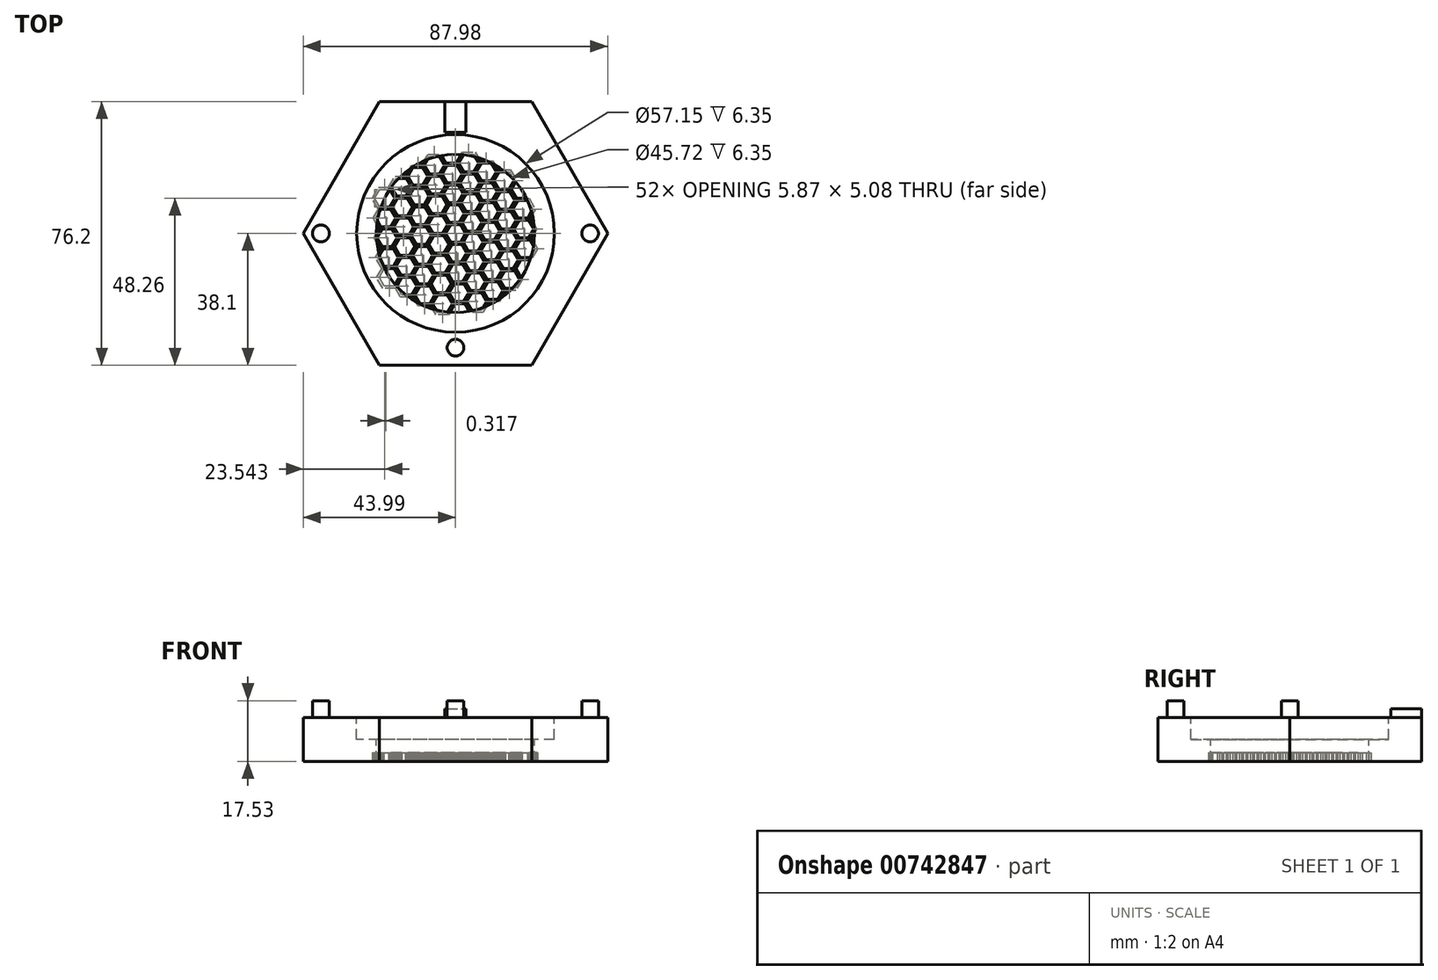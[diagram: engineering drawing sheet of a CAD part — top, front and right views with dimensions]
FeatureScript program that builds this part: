
annotation { "Feature Type Name" : "Feature", "Feature Type Description" : "" }
export const myFeature = defineFeature(function(context is Context, id is Id, definition is map)
    precondition{}
    {
        {
            var Q0;
            Q0=qCreatedBy(makeId("Top.planeOp"),FACE);
            var sketch = newSketch(context, id + "F0", { "sketchPlane" : qUnion([Q0])});
            skCircle(sketch, "E0.cCircle", {"center": v(0, 0) * mm, "radius": 38.1 * mm, "construction": true});
            skLineSegment(sketch, "E0.0", {"start": v(-22, 38.1) * mm, "end": v(22, 38.1) * mm});
            skLineSegment(sketch, "E0.1", {"start": v(22, 38.1) * mm, "end": v(44, 0) * mm});
            skLineSegment(sketch, "E0.2", {"start": v(44, 0) * mm, "end": v(22, -38.1) * mm});
            skLineSegment(sketch, "E0.3", {"start": v(22, -38.1) * mm, "end": v(-22, -38.1) * mm});
            skLineSegment(sketch, "E0.4", {"start": v(-22, -38.1) * mm, "end": v(-44, 0) * mm});
            skLineSegment(sketch, "E0.5", {"start": v(-44, 0) * mm, "end": v(-22, 38.1) * mm});
            skPoint(sketch, "E0.0.midPoint", {"position": v(0, 38.1) * mm});
            skSolve(sketch);
        }
        {
            var Q0;
            Q0 = qSketchRegion(id + "F0", true);
            extrude(context, id + "F1", {"entities" : qUnion([Q0]), "depth" : 12.7 * mm, "offsetDistance" : 25.4 * mm});
        }
        {
            var Q0;
            Q0=makeQuery(id+"F1.opExtrude","CAP_FACE",FACE,{"disambiguationData":[OSD([sQuery(id+"F0.wireOp",EDGE,"E0.0"),sQuery(id+"F0.wireOp",EDGE,"E0.1"),sQuery(id+"F0.wireOp",EDGE,"E0.2"),sQuery(id+"F0.wireOp",EDGE,"E0.3"),sQuery(id+"F0.wireOp",EDGE,"E0.4"),sQuery(id+"F0.wireOp",EDGE,"E0.5")])],"isStart":false});
            var sketch = newSketch(context, id + "F2", { "sketchPlane" : qUnion([Q0])});
            skCircle(sketch, "E1", {"center": v(0, 0) * mm, "radius": 28.58 * mm});
            skSolve(sketch);
        }
        {
            var Q0;
            Q0 = qSketchRegion(id + "F2", true);
            extrude(context, id + "F3", {"entities" : qUnion([Q0]), "operationType" : NewBodyOperationType.REMOVE, "oppositeDirection" : true, "depth" : 6.35 * mm, "offsetDistance" : 25.4 * mm});
        }
        {
            var Q0;
            Q0=makeQuery(id+"F3.boolean.opBoolean","COPY",FACE,{"derivedFrom":makeQuery(id+"F3.opExtrude","CAP_FACE",FACE,{"disambiguationData":[OSD([sQuery(id+"F2.wireOp",EDGE,"E1")])],"isStart":false})});
            var sketch = newSketch(context, id + "F4", { "sketchPlane" : qUnion([Q0])});
            skCircle(sketch, "E2", {"center": v(0, 0) * mm, "radius": 22.86 * mm});
            skSolve(sketch);
        }
        {
            var Q0;
            Q0 = qSketchRegion(id + "F4", true);
            extrude(context, id + "F5", {"entities" : qUnion([Q0]), "operationType" : NewBodyOperationType.REMOVE, "oppositeDirection" : true, "depth" : 25.4 * mm, "offsetDistance" : 25.4 * mm});
        }
        {
            var Q0;
            Q0=makeQuery(id+"F1.opExtrude","CAP_FACE",FACE,{"disambiguationData":[OSD([sQuery(id+"F0.wireOp",EDGE,"E0.0"),sQuery(id+"F0.wireOp",EDGE,"E0.1"),sQuery(id+"F0.wireOp",EDGE,"E0.2"),sQuery(id+"F0.wireOp",EDGE,"E0.3"),sQuery(id+"F0.wireOp",EDGE,"E0.4"),sQuery(id+"F0.wireOp",EDGE,"E0.5")])],"isStart":false});
            var sketch = newSketch(context, id + "F6", { "sketchPlane" : qUnion([Q0])});
            skCircle(sketch, "E3", {"center": v(0, -33.02) * mm, "radius": 2.41 * mm});
            skCircle(sketch, "E4", {"center": v(-38.91, 0) * mm, "radius": 2.41 * mm});
            skCircle(sketch, "E5", {"center": v(38.91, 0) * mm, "radius": 2.41 * mm});
            skSolve(sketch);
        }
        {
            var Q0;
            Q0 = qSketchRegion(id + "F6", true);
            extrude(context, id + "F7", {"entities" : qUnion([Q0]), "operationType" : NewBodyOperationType.ADD, "depth" : 4.83 * mm, "offsetDistance" : 25.4 * mm});
        }
        {
            var Q0;
            Q0=makeQuery(id+"F1.opExtrude","CAP_FACE",FACE,{"disambiguationData":[OSD([sQuery(id+"F0.wireOp",EDGE,"E0.0"),sQuery(id+"F0.wireOp",EDGE,"E0.1"),sQuery(id+"F0.wireOp",EDGE,"E0.2"),sQuery(id+"F0.wireOp",EDGE,"E0.3"),sQuery(id+"F0.wireOp",EDGE,"E0.4"),sQuery(id+"F0.wireOp",EDGE,"E0.5")])],"isStart":false});
            var sketch = newSketch(context, id + "F8", { "sketchPlane" : qUnion([Q0])});
            skLineSegment(sketch, "E6", {"start": v(0, 38.1) * mm, "end": v(-3.05, 38.1) * mm});
            skLineSegment(sketch, "E7", {"start": v(-3.05, 38.1) * mm, "end": v(-3.05, 29.21) * mm});
            skLineSegment(sketch, "E8", {"start": v(-3.05, 29.21) * mm, "end": v(3.05, 29.21) * mm});
            skLineSegment(sketch, "E9", {"start": v(3.05, 29.21) * mm, "end": v(3.05, 38.1) * mm});
            skLineSegment(sketch, "E10", {"start": v(3.05, 38.1) * mm, "end": v(0, 38.1) * mm});
            skSolve(sketch);
        }
        {
            var Q0;
            Q0 = qSketchRegion(id + "F8", true);
            extrude(context, id + "F9", {"entities" : qUnion([Q0]), "operationType" : NewBodyOperationType.ADD, "depth" : 2.54 * mm, "offsetDistance" : 25.4 * mm});
        }
        {
            var Q0;
            Q0=qCreatedBy(makeId("Top.planeOp"),FACE);
            var sketch = newSketch(context, id + "F10", { "sketchPlane" : qUnion([Q0])});
            skCircle(sketch, "E11.cCircle", {"center": v(0, 0) * mm, "radius": 3.18 * mm, "construction": true});
            skLineSegment(sketch, "E11.0", {"start": v(-1.83, 3.18) * mm, "end": v(1.83, 3.18) * mm});
            skLineSegment(sketch, "E11.1", {"start": v(1.83, 3.18) * mm, "end": v(3.67, 0) * mm});
            skLineSegment(sketch, "E11.2", {"start": v(3.67, 0) * mm, "end": v(1.83, -3.17) * mm});
            skLineSegment(sketch, "E11.3", {"start": v(1.83, -3.17) * mm, "end": v(-1.83, -3.18) * mm});
            skLineSegment(sketch, "E11.4", {"start": v(-1.83, -3.18) * mm, "end": v(-3.67, 0) * mm});
            skLineSegment(sketch, "E11.5", {"start": v(-3.67, 0) * mm, "end": v(-1.83, 3.18) * mm});
            skPoint(sketch, "E11.0.midPoint", {"position": v(0, 3.18) * mm});
            skSolve(sketch);
        }
        {
            var Q0;
            Q0 = qSketchRegion(id + "F10", true);
            extrude(context, id + "F11", {"entities" : qUnion([Q0]), "depth" : 2.54 * mm, "offsetDistance" : 25.4 * mm});
        }
        {
            var Q0;
            Q0=makeQuery(id+"F11.opExtrude","CAP_FACE",FACE,{"disambiguationData":[OSD([sQuery(id+"F10.wireOp",EDGE,"E11.0"),sQuery(id+"F10.wireOp",EDGE,"E11.1"),sQuery(id+"F10.wireOp",EDGE,"E11.2"),sQuery(id+"F10.wireOp",EDGE,"E11.3"),sQuery(id+"F10.wireOp",EDGE,"E11.4"),sQuery(id+"F10.wireOp",EDGE,"E11.5")])],"isStart":false});
            var sketch = newSketch(context, id + "F12", { "sketchPlane" : qUnion([Q0])});
            skCircle(sketch, "E12.cCircle", {"center": v(0, 0) * mm, "radius": 2.54 * mm, "construction": true});
            skLineSegment(sketch, "E12.0", {"start": v(-1.47, 2.54) * mm, "end": v(1.47, 2.54) * mm});
            skLineSegment(sketch, "E12.1", {"start": v(1.47, 2.54) * mm, "end": v(2.93, 0) * mm});
            skLineSegment(sketch, "E12.2", {"start": v(2.93, 0) * mm, "end": v(1.47, -2.54) * mm});
            skLineSegment(sketch, "E12.3", {"start": v(1.47, -2.54) * mm, "end": v(-1.47, -2.54) * mm});
            skLineSegment(sketch, "E12.4", {"start": v(-1.47, -2.54) * mm, "end": v(-2.93, 0) * mm});
            skLineSegment(sketch, "E12.5", {"start": v(-2.93, 0) * mm, "end": v(-1.47, 2.54) * mm});
            skPoint(sketch, "E12.0.midPoint", {"position": v(0, 2.54) * mm});
            skSolve(sketch);
        }
        {
            var Q0;
            Q0 = qSketchRegion(id + "F12", true);
            extrude(context, id + "F13", {"entities" : qUnion([Q0]), "operationType" : NewBodyOperationType.REMOVE, "oppositeDirection" : true, "depth" : 25.4 * mm, "offsetDistance" : 25.4 * mm});
        }
        {
            var Q0;
            Q0=makeQuery(id+"F11.opExtrude","SWEPT_BODY",BODY,{"disambiguationData":[OSD([sQuery(id+"F10.wireOp",EDGE,"E11.0"),sQuery(id+"F10.wireOp",EDGE,"E11.1"),sQuery(id+"F10.wireOp",EDGE,"E11.2"),sQuery(id+"F10.wireOp",EDGE,"E11.3"),sQuery(id+"F10.wireOp",EDGE,"E11.4"),sQuery(id+"F10.wireOp",EDGE,"E11.5")])]});
            transform(context, id + "F14", {"entities" : qUnion([Q0]), "transformType" : TransformType.TRANSLATION_3D, "dx" : 4.76 * mm, "dy" : 3.17 * mm, "dz" : 0 * mm, "makeCopy" : true});
        }
        {
            var Q0;
            Q0=makeQuery(id+"F11.opExtrude","SWEPT_BODY",BODY,{"disambiguationData":[OSD([sQuery(id+"F10.wireOp",EDGE,"E11.0"),sQuery(id+"F10.wireOp",EDGE,"E11.1"),sQuery(id+"F10.wireOp",EDGE,"E11.2"),sQuery(id+"F10.wireOp",EDGE,"E11.3"),sQuery(id+"F10.wireOp",EDGE,"E11.4"),sQuery(id+"F10.wireOp",EDGE,"E11.5")])]});
            var Q1;
            Q1=makeQuery(id+"F14.opPattern","COPY",BODY,{"derivedFrom":makeQuery(id+"F11.opExtrude","SWEPT_BODY",BODY,{"disambiguationData":[OSD([sQuery(id+"F10.wireOp",EDGE,"E11.0"),sQuery(id+"F10.wireOp",EDGE,"E11.1"),sQuery(id+"F10.wireOp",EDGE,"E11.2"),sQuery(id+"F10.wireOp",EDGE,"E11.3"),sQuery(id+"F10.wireOp",EDGE,"E11.4"),sQuery(id+"F10.wireOp",EDGE,"E11.5")])]}),"instanceName":"1"});
            transform(context, id + "F15", {"entities" : qUnion([Q0, Q1]), "transformType" : TransformType.TRANSLATION_3D, "dx" : -5.08 * mm, "dy" : 2.54 * mm, "dz" : 0 * mm, "makeCopy" : true});
        }
        {
            var Q0;
            Q0=makeQuery(id+"F15.opPattern","COPY",BODY,{"derivedFrom":makeQuery(id+"F14.opPattern","COPY",BODY,{"derivedFrom":makeQuery(id+"F11.opExtrude","SWEPT_BODY",BODY,{"disambiguationData":[OSD([sQuery(id+"F10.wireOp",EDGE,"E11.0"),sQuery(id+"F10.wireOp",EDGE,"E11.1"),sQuery(id+"F10.wireOp",EDGE,"E11.2"),sQuery(id+"F10.wireOp",EDGE,"E11.3"),sQuery(id+"F10.wireOp",EDGE,"E11.4"),sQuery(id+"F10.wireOp",EDGE,"E11.5")])]}),"instanceName":"1"}),"instanceName":"1"});
            var Q1;
            Q1=makeQuery(id+"F14.opPattern","COPY",BODY,{"derivedFrom":makeQuery(id+"F11.opExtrude","SWEPT_BODY",BODY,{"disambiguationData":[OSD([sQuery(id+"F10.wireOp",EDGE,"E11.0"),sQuery(id+"F10.wireOp",EDGE,"E11.1"),sQuery(id+"F10.wireOp",EDGE,"E11.2"),sQuery(id+"F10.wireOp",EDGE,"E11.3"),sQuery(id+"F10.wireOp",EDGE,"E11.4"),sQuery(id+"F10.wireOp",EDGE,"E11.5")])]}),"instanceName":"1"});
            var Q2;
            Q2=makeQuery(id+"F15.opPattern","COPY",BODY,{"derivedFrom":makeQuery(id+"F11.opExtrude","SWEPT_BODY",BODY,{"disambiguationData":[OSD([sQuery(id+"F10.wireOp",EDGE,"E11.0"),sQuery(id+"F10.wireOp",EDGE,"E11.1"),sQuery(id+"F10.wireOp",EDGE,"E11.2"),sQuery(id+"F10.wireOp",EDGE,"E11.3"),sQuery(id+"F10.wireOp",EDGE,"E11.4"),sQuery(id+"F10.wireOp",EDGE,"E11.5")])]}),"instanceName":"1"});
            var Q3;
            Q3=makeQuery(id+"F11.opExtrude","SWEPT_BODY",BODY,{"disambiguationData":[OSD([sQuery(id+"F10.wireOp",EDGE,"E11.0"),sQuery(id+"F10.wireOp",EDGE,"E11.1"),sQuery(id+"F10.wireOp",EDGE,"E11.2"),sQuery(id+"F10.wireOp",EDGE,"E11.3"),sQuery(id+"F10.wireOp",EDGE,"E11.4"),sQuery(id+"F10.wireOp",EDGE,"E11.5")])]});
            transform(context, id + "F16", {"entities" : qUnion([Q0, Q1, Q2, Q3]), "transformType" : TransformType.TRANSLATION_3D, "dx" : 9.52 * mm, "dy" : 6.35 * mm, "dz" : 0 * mm, "makeCopy" : true});
        }
        {
            var Q0;
            Q0=makeQuery(id+"F16.opPattern","COPY",BODY,{"derivedFrom":makeQuery(id+"F15.opPattern","COPY",BODY,{"derivedFrom":makeQuery(id+"F11.opExtrude","SWEPT_BODY",BODY,{"disambiguationData":[OSD([sQuery(id+"F10.wireOp",EDGE,"E11.0"),sQuery(id+"F10.wireOp",EDGE,"E11.1"),sQuery(id+"F10.wireOp",EDGE,"E11.2"),sQuery(id+"F10.wireOp",EDGE,"E11.3"),sQuery(id+"F10.wireOp",EDGE,"E11.4"),sQuery(id+"F10.wireOp",EDGE,"E11.5")])]}),"instanceName":"1"}),"instanceName":"1"});
            var Q1;
            Q1=makeQuery(id+"F11.opExtrude","SWEPT_BODY",BODY,{"disambiguationData":[OSD([sQuery(id+"F10.wireOp",EDGE,"E11.0"),sQuery(id+"F10.wireOp",EDGE,"E11.1"),sQuery(id+"F10.wireOp",EDGE,"E11.2"),sQuery(id+"F10.wireOp",EDGE,"E11.3"),sQuery(id+"F10.wireOp",EDGE,"E11.4"),sQuery(id+"F10.wireOp",EDGE,"E11.5")])]});
            var Q2;
            Q2=makeQuery(id+"F14.opPattern","COPY",BODY,{"derivedFrom":makeQuery(id+"F11.opExtrude","SWEPT_BODY",BODY,{"disambiguationData":[OSD([sQuery(id+"F10.wireOp",EDGE,"E11.0"),sQuery(id+"F10.wireOp",EDGE,"E11.1"),sQuery(id+"F10.wireOp",EDGE,"E11.2"),sQuery(id+"F10.wireOp",EDGE,"E11.3"),sQuery(id+"F10.wireOp",EDGE,"E11.4"),sQuery(id+"F10.wireOp",EDGE,"E11.5")])]}),"instanceName":"1"});
            var Q3;
            Q3=makeQuery(id+"F16.opPattern","COPY",BODY,{"derivedFrom":makeQuery(id+"F11.opExtrude","SWEPT_BODY",BODY,{"disambiguationData":[OSD([sQuery(id+"F10.wireOp",EDGE,"E11.0"),sQuery(id+"F10.wireOp",EDGE,"E11.1"),sQuery(id+"F10.wireOp",EDGE,"E11.2"),sQuery(id+"F10.wireOp",EDGE,"E11.3"),sQuery(id+"F10.wireOp",EDGE,"E11.4"),sQuery(id+"F10.wireOp",EDGE,"E11.5")])]}),"instanceName":"1"});
            var Q4;
            Q4=makeQuery(id+"F16.opPattern","COPY",BODY,{"derivedFrom":makeQuery(id+"F15.opPattern","COPY",BODY,{"derivedFrom":makeQuery(id+"F14.opPattern","COPY",BODY,{"derivedFrom":makeQuery(id+"F11.opExtrude","SWEPT_BODY",BODY,{"disambiguationData":[OSD([sQuery(id+"F10.wireOp",EDGE,"E11.0"),sQuery(id+"F10.wireOp",EDGE,"E11.1"),sQuery(id+"F10.wireOp",EDGE,"E11.2"),sQuery(id+"F10.wireOp",EDGE,"E11.3"),sQuery(id+"F10.wireOp",EDGE,"E11.4"),sQuery(id+"F10.wireOp",EDGE,"E11.5")])]}),"instanceName":"1"}),"instanceName":"1"}),"instanceName":"1"});
            var Q5;
            Q5=makeQuery(id+"F16.opPattern","COPY",BODY,{"derivedFrom":makeQuery(id+"F14.opPattern","COPY",BODY,{"derivedFrom":makeQuery(id+"F11.opExtrude","SWEPT_BODY",BODY,{"disambiguationData":[OSD([sQuery(id+"F10.wireOp",EDGE,"E11.0"),sQuery(id+"F10.wireOp",EDGE,"E11.1"),sQuery(id+"F10.wireOp",EDGE,"E11.2"),sQuery(id+"F10.wireOp",EDGE,"E11.3"),sQuery(id+"F10.wireOp",EDGE,"E11.4"),sQuery(id+"F10.wireOp",EDGE,"E11.5")])]}),"instanceName":"1"}),"instanceName":"1"});
            var Q6;
            Q6=makeQuery(id+"F15.opPattern","COPY",BODY,{"derivedFrom":makeQuery(id+"F14.opPattern","COPY",BODY,{"derivedFrom":makeQuery(id+"F11.opExtrude","SWEPT_BODY",BODY,{"disambiguationData":[OSD([sQuery(id+"F10.wireOp",EDGE,"E11.0"),sQuery(id+"F10.wireOp",EDGE,"E11.1"),sQuery(id+"F10.wireOp",EDGE,"E11.2"),sQuery(id+"F10.wireOp",EDGE,"E11.3"),sQuery(id+"F10.wireOp",EDGE,"E11.4"),sQuery(id+"F10.wireOp",EDGE,"E11.5")])]}),"instanceName":"1"}),"instanceName":"1"});
            var Q7;
            Q7=makeQuery(id+"F15.opPattern","COPY",BODY,{"derivedFrom":makeQuery(id+"F11.opExtrude","SWEPT_BODY",BODY,{"disambiguationData":[OSD([sQuery(id+"F10.wireOp",EDGE,"E11.0"),sQuery(id+"F10.wireOp",EDGE,"E11.1"),sQuery(id+"F10.wireOp",EDGE,"E11.2"),sQuery(id+"F10.wireOp",EDGE,"E11.3"),sQuery(id+"F10.wireOp",EDGE,"E11.4"),sQuery(id+"F10.wireOp",EDGE,"E11.5")])]}),"instanceName":"1"});
            transform(context, id + "F17", {"entities" : qUnion([Q0, Q1, Q2, Q3, Q4, Q5, Q6, Q7]), "transformType" : TransformType.TRANSLATION_3D, "dx" : 0.66 * mm, "dy" : -11.43 * mm, "dz" : 0 * mm, "makeCopy" : true});
        }
        {
            var Q0;
            Q0=makeQuery(id+"F17.opPattern","COPY",BODY,{"derivedFrom":makeQuery(id+"F15.opPattern","COPY",BODY,{"derivedFrom":makeQuery(id+"F14.opPattern","COPY",BODY,{"derivedFrom":makeQuery(id+"F11.opExtrude","SWEPT_BODY",BODY,{"disambiguationData":[OSD([sQuery(id+"F10.wireOp",EDGE,"E11.0"),sQuery(id+"F10.wireOp",EDGE,"E11.1"),sQuery(id+"F10.wireOp",EDGE,"E11.2"),sQuery(id+"F10.wireOp",EDGE,"E11.3"),sQuery(id+"F10.wireOp",EDGE,"E11.4"),sQuery(id+"F10.wireOp",EDGE,"E11.5")])]}),"instanceName":"1"}),"instanceName":"1"}),"instanceName":"1"});
            var Q1;
            Q1=makeQuery(id+"F17.opPattern","COPY",BODY,{"derivedFrom":makeQuery(id+"F14.opPattern","COPY",BODY,{"derivedFrom":makeQuery(id+"F11.opExtrude","SWEPT_BODY",BODY,{"disambiguationData":[OSD([sQuery(id+"F10.wireOp",EDGE,"E11.0"),sQuery(id+"F10.wireOp",EDGE,"E11.1"),sQuery(id+"F10.wireOp",EDGE,"E11.2"),sQuery(id+"F10.wireOp",EDGE,"E11.3"),sQuery(id+"F10.wireOp",EDGE,"E11.4"),sQuery(id+"F10.wireOp",EDGE,"E11.5")])]}),"instanceName":"1"}),"instanceName":"1"});
            var Q2;
            Q2=makeQuery(id+"F17.opPattern","COPY",BODY,{"derivedFrom":makeQuery(id+"F16.opPattern","COPY",BODY,{"derivedFrom":makeQuery(id+"F11.opExtrude","SWEPT_BODY",BODY,{"disambiguationData":[OSD([sQuery(id+"F10.wireOp",EDGE,"E11.0"),sQuery(id+"F10.wireOp",EDGE,"E11.1"),sQuery(id+"F10.wireOp",EDGE,"E11.2"),sQuery(id+"F10.wireOp",EDGE,"E11.3"),sQuery(id+"F10.wireOp",EDGE,"E11.4"),sQuery(id+"F10.wireOp",EDGE,"E11.5")])]}),"instanceName":"1"}),"instanceName":"1"});
            var Q3;
            Q3=makeQuery(id+"F17.opPattern","COPY",BODY,{"derivedFrom":makeQuery(id+"F16.opPattern","COPY",BODY,{"derivedFrom":makeQuery(id+"F15.opPattern","COPY",BODY,{"derivedFrom":makeQuery(id+"F11.opExtrude","SWEPT_BODY",BODY,{"disambiguationData":[OSD([sQuery(id+"F10.wireOp",EDGE,"E11.0"),sQuery(id+"F10.wireOp",EDGE,"E11.1"),sQuery(id+"F10.wireOp",EDGE,"E11.2"),sQuery(id+"F10.wireOp",EDGE,"E11.3"),sQuery(id+"F10.wireOp",EDGE,"E11.4"),sQuery(id+"F10.wireOp",EDGE,"E11.5")])]}),"instanceName":"1"}),"instanceName":"1"}),"instanceName":"1"});
            var Q4;
            Q4=makeQuery(id+"F17.opPattern","COPY",BODY,{"derivedFrom":makeQuery(id+"F16.opPattern","COPY",BODY,{"derivedFrom":makeQuery(id+"F15.opPattern","COPY",BODY,{"derivedFrom":makeQuery(id+"F14.opPattern","COPY",BODY,{"derivedFrom":makeQuery(id+"F11.opExtrude","SWEPT_BODY",BODY,{"disambiguationData":[OSD([sQuery(id+"F10.wireOp",EDGE,"E11.0"),sQuery(id+"F10.wireOp",EDGE,"E11.1"),sQuery(id+"F10.wireOp",EDGE,"E11.2"),sQuery(id+"F10.wireOp",EDGE,"E11.3"),sQuery(id+"F10.wireOp",EDGE,"E11.4"),sQuery(id+"F10.wireOp",EDGE,"E11.5")])]}),"instanceName":"1"}),"instanceName":"1"}),"instanceName":"1"}),"instanceName":"1"});
            var Q5;
            Q5=makeQuery(id+"F17.opPattern","COPY",BODY,{"derivedFrom":makeQuery(id+"F15.opPattern","COPY",BODY,{"derivedFrom":makeQuery(id+"F11.opExtrude","SWEPT_BODY",BODY,{"disambiguationData":[OSD([sQuery(id+"F10.wireOp",EDGE,"E11.0"),sQuery(id+"F10.wireOp",EDGE,"E11.1"),sQuery(id+"F10.wireOp",EDGE,"E11.2"),sQuery(id+"F10.wireOp",EDGE,"E11.3"),sQuery(id+"F10.wireOp",EDGE,"E11.4"),sQuery(id+"F10.wireOp",EDGE,"E11.5")])]}),"instanceName":"1"}),"instanceName":"1"});
            var Q6;
            Q6=makeQuery(id+"F17.opPattern","COPY",BODY,{"derivedFrom":makeQuery(id+"F16.opPattern","COPY",BODY,{"derivedFrom":makeQuery(id+"F14.opPattern","COPY",BODY,{"derivedFrom":makeQuery(id+"F11.opExtrude","SWEPT_BODY",BODY,{"disambiguationData":[OSD([sQuery(id+"F10.wireOp",EDGE,"E11.0"),sQuery(id+"F10.wireOp",EDGE,"E11.1"),sQuery(id+"F10.wireOp",EDGE,"E11.2"),sQuery(id+"F10.wireOp",EDGE,"E11.3"),sQuery(id+"F10.wireOp",EDGE,"E11.4"),sQuery(id+"F10.wireOp",EDGE,"E11.5")])]}),"instanceName":"1"}),"instanceName":"1"}),"instanceName":"1"});
            transform(context, id + "F18", {"entities" : qUnion([Q0, Q1, Q2, Q3, Q4, Q5, Q6]), "transformType" : TransformType.TRANSLATION_3D, "dx" : 0.64 * mm, "dy" : -11.43 * mm, "dz" : 0 * mm, "makeCopy" : true});
        }
        {
            var Q0;
            Q0=makeQuery(id+"F17.opPattern","COPY",BODY,{"derivedFrom":makeQuery(id+"F16.opPattern","COPY",BODY,{"derivedFrom":makeQuery(id+"F11.opExtrude","SWEPT_BODY",BODY,{"disambiguationData":[OSD([sQuery(id+"F10.wireOp",EDGE,"E11.0"),sQuery(id+"F10.wireOp",EDGE,"E11.1"),sQuery(id+"F10.wireOp",EDGE,"E11.2"),sQuery(id+"F10.wireOp",EDGE,"E11.3"),sQuery(id+"F10.wireOp",EDGE,"E11.4"),sQuery(id+"F10.wireOp",EDGE,"E11.5")])]}),"instanceName":"1"}),"instanceName":"1"});
            var Q1;
            Q1=makeQuery(id+"F17.opPattern","COPY",BODY,{"derivedFrom":makeQuery(id+"F16.opPattern","COPY",BODY,{"derivedFrom":makeQuery(id+"F14.opPattern","COPY",BODY,{"derivedFrom":makeQuery(id+"F11.opExtrude","SWEPT_BODY",BODY,{"disambiguationData":[OSD([sQuery(id+"F10.wireOp",EDGE,"E11.0"),sQuery(id+"F10.wireOp",EDGE,"E11.1"),sQuery(id+"F10.wireOp",EDGE,"E11.2"),sQuery(id+"F10.wireOp",EDGE,"E11.3"),sQuery(id+"F10.wireOp",EDGE,"E11.4"),sQuery(id+"F10.wireOp",EDGE,"E11.5")])]}),"instanceName":"1"}),"instanceName":"1"}),"instanceName":"1"});
            transform(context, id + "F19", {"entities" : qUnion([Q0, Q1]), "transformType" : TransformType.TRANSLATION_3D, "dx" : 5.08 * mm, "dy" : -2.54 * mm, "dz" : 0 * mm, "makeCopy" : true});
        }
        {
            var Q0;
            Q0=makeQuery(id+"F17.opPattern","COPY",BODY,{"derivedFrom":makeQuery(id+"F16.opPattern","COPY",BODY,{"derivedFrom":makeQuery(id+"F14.opPattern","COPY",BODY,{"derivedFrom":makeQuery(id+"F11.opExtrude","SWEPT_BODY",BODY,{"disambiguationData":[OSD([sQuery(id+"F10.wireOp",EDGE,"E11.0"),sQuery(id+"F10.wireOp",EDGE,"E11.1"),sQuery(id+"F10.wireOp",EDGE,"E11.2"),sQuery(id+"F10.wireOp",EDGE,"E11.3"),sQuery(id+"F10.wireOp",EDGE,"E11.4"),sQuery(id+"F10.wireOp",EDGE,"E11.5")])]}),"instanceName":"1"}),"instanceName":"1"}),"instanceName":"1"});
            var Q1;
            Q1=makeQuery(id+"F17.opPattern","COPY",BODY,{"derivedFrom":makeQuery(id+"F16.opPattern","COPY",BODY,{"derivedFrom":makeQuery(id+"F15.opPattern","COPY",BODY,{"derivedFrom":makeQuery(id+"F14.opPattern","COPY",BODY,{"derivedFrom":makeQuery(id+"F11.opExtrude","SWEPT_BODY",BODY,{"disambiguationData":[OSD([sQuery(id+"F10.wireOp",EDGE,"E11.0"),sQuery(id+"F10.wireOp",EDGE,"E11.1"),sQuery(id+"F10.wireOp",EDGE,"E11.2"),sQuery(id+"F10.wireOp",EDGE,"E11.3"),sQuery(id+"F10.wireOp",EDGE,"E11.4"),sQuery(id+"F10.wireOp",EDGE,"E11.5")])]}),"instanceName":"1"}),"instanceName":"1"}),"instanceName":"1"}),"instanceName":"1"});
            var Q2;
            Q2=makeQuery(id+"F16.opPattern","COPY",BODY,{"derivedFrom":makeQuery(id+"F15.opPattern","COPY",BODY,{"derivedFrom":makeQuery(id+"F14.opPattern","COPY",BODY,{"derivedFrom":makeQuery(id+"F11.opExtrude","SWEPT_BODY",BODY,{"disambiguationData":[OSD([sQuery(id+"F10.wireOp",EDGE,"E11.0"),sQuery(id+"F10.wireOp",EDGE,"E11.1"),sQuery(id+"F10.wireOp",EDGE,"E11.2"),sQuery(id+"F10.wireOp",EDGE,"E11.3"),sQuery(id+"F10.wireOp",EDGE,"E11.4"),sQuery(id+"F10.wireOp",EDGE,"E11.5")])]}),"instanceName":"1"}),"instanceName":"1"}),"instanceName":"1"});
            transform(context, id + "F20", {"entities" : qUnion([Q0, Q1, Q2]), "transformType" : TransformType.TRANSLATION_3D, "dx" : 4.78 * mm, "dy" : 3.17 * mm, "dz" : 0 * mm, "makeCopy" : true});
        }
        {
            var Q0;
            Q0=makeQuery(id+"F16.opPattern","COPY",BODY,{"derivedFrom":makeQuery(id+"F15.opPattern","COPY",BODY,{"derivedFrom":makeQuery(id+"F11.opExtrude","SWEPT_BODY",BODY,{"disambiguationData":[OSD([sQuery(id+"F10.wireOp",EDGE,"E11.0"),sQuery(id+"F10.wireOp",EDGE,"E11.1"),sQuery(id+"F10.wireOp",EDGE,"E11.2"),sQuery(id+"F10.wireOp",EDGE,"E11.3"),sQuery(id+"F10.wireOp",EDGE,"E11.4"),sQuery(id+"F10.wireOp",EDGE,"E11.5")])]}),"instanceName":"1"}),"instanceName":"1"});
            var Q1;
            Q1=makeQuery(id+"F14.opPattern","COPY",BODY,{"derivedFrom":makeQuery(id+"F11.opExtrude","SWEPT_BODY",BODY,{"disambiguationData":[OSD([sQuery(id+"F10.wireOp",EDGE,"E11.0"),sQuery(id+"F10.wireOp",EDGE,"E11.1"),sQuery(id+"F10.wireOp",EDGE,"E11.2"),sQuery(id+"F10.wireOp",EDGE,"E11.3"),sQuery(id+"F10.wireOp",EDGE,"E11.4"),sQuery(id+"F10.wireOp",EDGE,"E11.5")])]}),"instanceName":"1"});
            var Q2;
            Q2=makeQuery(id+"F16.opPattern","COPY",BODY,{"derivedFrom":makeQuery(id+"F11.opExtrude","SWEPT_BODY",BODY,{"disambiguationData":[OSD([sQuery(id+"F10.wireOp",EDGE,"E11.0"),sQuery(id+"F10.wireOp",EDGE,"E11.1"),sQuery(id+"F10.wireOp",EDGE,"E11.2"),sQuery(id+"F10.wireOp",EDGE,"E11.3"),sQuery(id+"F10.wireOp",EDGE,"E11.4"),sQuery(id+"F10.wireOp",EDGE,"E11.5")])]}),"instanceName":"1"});
            var Q3;
            Q3=makeQuery(id+"F19.opPattern","COPY",BODY,{"derivedFrom":makeQuery(id+"F17.opPattern","COPY",BODY,{"derivedFrom":makeQuery(id+"F16.opPattern","COPY",BODY,{"derivedFrom":makeQuery(id+"F14.opPattern","COPY",BODY,{"derivedFrom":makeQuery(id+"F11.opExtrude","SWEPT_BODY",BODY,{"disambiguationData":[OSD([sQuery(id+"F10.wireOp",EDGE,"E11.0"),sQuery(id+"F10.wireOp",EDGE,"E11.1"),sQuery(id+"F10.wireOp",EDGE,"E11.2"),sQuery(id+"F10.wireOp",EDGE,"E11.3"),sQuery(id+"F10.wireOp",EDGE,"E11.4"),sQuery(id+"F10.wireOp",EDGE,"E11.5")])]}),"instanceName":"1"}),"instanceName":"1"}),"instanceName":"1"}),"instanceName":"1"});
            var Q4;
            Q4=makeQuery(id+"F15.opPattern","COPY",BODY,{"derivedFrom":makeQuery(id+"F14.opPattern","COPY",BODY,{"derivedFrom":makeQuery(id+"F11.opExtrude","SWEPT_BODY",BODY,{"disambiguationData":[OSD([sQuery(id+"F10.wireOp",EDGE,"E11.0"),sQuery(id+"F10.wireOp",EDGE,"E11.1"),sQuery(id+"F10.wireOp",EDGE,"E11.2"),sQuery(id+"F10.wireOp",EDGE,"E11.3"),sQuery(id+"F10.wireOp",EDGE,"E11.4"),sQuery(id+"F10.wireOp",EDGE,"E11.5")])]}),"instanceName":"1"}),"instanceName":"1"});
            var Q5;
            Q5=makeQuery(id+"F11.opExtrude","SWEPT_BODY",BODY,{"disambiguationData":[OSD([sQuery(id+"F10.wireOp",EDGE,"E11.0"),sQuery(id+"F10.wireOp",EDGE,"E11.1"),sQuery(id+"F10.wireOp",EDGE,"E11.2"),sQuery(id+"F10.wireOp",EDGE,"E11.3"),sQuery(id+"F10.wireOp",EDGE,"E11.4"),sQuery(id+"F10.wireOp",EDGE,"E11.5")])]});
            var Q6;
            Q6=makeQuery(id+"F15.opPattern","COPY",BODY,{"derivedFrom":makeQuery(id+"F11.opExtrude","SWEPT_BODY",BODY,{"disambiguationData":[OSD([sQuery(id+"F10.wireOp",EDGE,"E11.0"),sQuery(id+"F10.wireOp",EDGE,"E11.1"),sQuery(id+"F10.wireOp",EDGE,"E11.2"),sQuery(id+"F10.wireOp",EDGE,"E11.3"),sQuery(id+"F10.wireOp",EDGE,"E11.4"),sQuery(id+"F10.wireOp",EDGE,"E11.5")])]}),"instanceName":"1"});
            transform(context, id + "F21", {"entities" : qUnion([Q0, Q1, Q2, Q3, Q4, Q5, Q6]), "transformType" : TransformType.TRANSLATION_3D, "dx" : -0.64 * mm, "dy" : 11.43 * mm, "dz" : 0 * mm, "makeCopy" : true});
        }
        {
            var Q0;
            Q0=makeQuery(id+"F18.opPattern","COPY",BODY,{"derivedFrom":makeQuery(id+"F17.opPattern","COPY",BODY,{"derivedFrom":makeQuery(id+"F15.opPattern","COPY",BODY,{"derivedFrom":makeQuery(id+"F14.opPattern","COPY",BODY,{"derivedFrom":makeQuery(id+"F11.opExtrude","SWEPT_BODY",BODY,{"disambiguationData":[OSD([sQuery(id+"F10.wireOp",EDGE,"E11.0"),sQuery(id+"F10.wireOp",EDGE,"E11.1"),sQuery(id+"F10.wireOp",EDGE,"E11.2"),sQuery(id+"F10.wireOp",EDGE,"E11.3"),sQuery(id+"F10.wireOp",EDGE,"E11.4"),sQuery(id+"F10.wireOp",EDGE,"E11.5")])]}),"instanceName":"1"}),"instanceName":"1"}),"instanceName":"1"}),"instanceName":"1"});
            var Q1;
            Q1=makeQuery(id+"F17.opPattern","COPY",BODY,{"derivedFrom":makeQuery(id+"F11.opExtrude","SWEPT_BODY",BODY,{"disambiguationData":[OSD([sQuery(id+"F10.wireOp",EDGE,"E11.0"),sQuery(id+"F10.wireOp",EDGE,"E11.1"),sQuery(id+"F10.wireOp",EDGE,"E11.2"),sQuery(id+"F10.wireOp",EDGE,"E11.3"),sQuery(id+"F10.wireOp",EDGE,"E11.4"),sQuery(id+"F10.wireOp",EDGE,"E11.5")])]}),"instanceName":"1"});
            var Q2;
            Q2=makeQuery(id+"F17.opPattern","COPY",BODY,{"derivedFrom":makeQuery(id+"F15.opPattern","COPY",BODY,{"derivedFrom":makeQuery(id+"F14.opPattern","COPY",BODY,{"derivedFrom":makeQuery(id+"F11.opExtrude","SWEPT_BODY",BODY,{"disambiguationData":[OSD([sQuery(id+"F10.wireOp",EDGE,"E11.0"),sQuery(id+"F10.wireOp",EDGE,"E11.1"),sQuery(id+"F10.wireOp",EDGE,"E11.2"),sQuery(id+"F10.wireOp",EDGE,"E11.3"),sQuery(id+"F10.wireOp",EDGE,"E11.4"),sQuery(id+"F10.wireOp",EDGE,"E11.5")])]}),"instanceName":"1"}),"instanceName":"1"}),"instanceName":"1"});
            var Q3;
            Q3=makeQuery(id+"F11.opExtrude","SWEPT_BODY",BODY,{"disambiguationData":[OSD([sQuery(id+"F10.wireOp",EDGE,"E11.0"),sQuery(id+"F10.wireOp",EDGE,"E11.1"),sQuery(id+"F10.wireOp",EDGE,"E11.2"),sQuery(id+"F10.wireOp",EDGE,"E11.3"),sQuery(id+"F10.wireOp",EDGE,"E11.4"),sQuery(id+"F10.wireOp",EDGE,"E11.5")])]});
            var Q4;
            Q4=makeQuery(id+"F15.opPattern","COPY",BODY,{"derivedFrom":makeQuery(id+"F14.opPattern","COPY",BODY,{"derivedFrom":makeQuery(id+"F11.opExtrude","SWEPT_BODY",BODY,{"disambiguationData":[OSD([sQuery(id+"F10.wireOp",EDGE,"E11.0"),sQuery(id+"F10.wireOp",EDGE,"E11.1"),sQuery(id+"F10.wireOp",EDGE,"E11.2"),sQuery(id+"F10.wireOp",EDGE,"E11.3"),sQuery(id+"F10.wireOp",EDGE,"E11.4"),sQuery(id+"F10.wireOp",EDGE,"E11.5")])]}),"instanceName":"1"}),"instanceName":"1"});
            var Q5;
            Q5=makeQuery(id+"F21.opPattern","COPY",BODY,{"derivedFrom":makeQuery(id+"F11.opExtrude","SWEPT_BODY",BODY,{"disambiguationData":[OSD([sQuery(id+"F10.wireOp",EDGE,"E11.0"),sQuery(id+"F10.wireOp",EDGE,"E11.1"),sQuery(id+"F10.wireOp",EDGE,"E11.2"),sQuery(id+"F10.wireOp",EDGE,"E11.3"),sQuery(id+"F10.wireOp",EDGE,"E11.4"),sQuery(id+"F10.wireOp",EDGE,"E11.5")])]}),"instanceName":"1"});
            var Q6;
            Q6=makeQuery(id+"F21.opPattern","COPY",BODY,{"derivedFrom":makeQuery(id+"F15.opPattern","COPY",BODY,{"derivedFrom":makeQuery(id+"F14.opPattern","COPY",BODY,{"derivedFrom":makeQuery(id+"F11.opExtrude","SWEPT_BODY",BODY,{"disambiguationData":[OSD([sQuery(id+"F10.wireOp",EDGE,"E11.0"),sQuery(id+"F10.wireOp",EDGE,"E11.1"),sQuery(id+"F10.wireOp",EDGE,"E11.2"),sQuery(id+"F10.wireOp",EDGE,"E11.3"),sQuery(id+"F10.wireOp",EDGE,"E11.4"),sQuery(id+"F10.wireOp",EDGE,"E11.5")])]}),"instanceName":"1"}),"instanceName":"1"}),"instanceName":"1"});
            transform(context, id + "F22", {"entities" : qUnion([Q0, Q1, Q2, Q3, Q4, Q5, Q6]), "transformType" : TransformType.TRANSLATION_3D, "dx" : -9.9 * mm, "dy" : -0.64 * mm, "dz" : 0 * mm, "makeCopy" : true});
        }
        {
            var Q0;
            Q0=makeQuery(id+"F17.opPattern","COPY",BODY,{"derivedFrom":makeQuery(id+"F15.opPattern","COPY",BODY,{"derivedFrom":makeQuery(id+"F11.opExtrude","SWEPT_BODY",BODY,{"disambiguationData":[OSD([sQuery(id+"F10.wireOp",EDGE,"E11.0"),sQuery(id+"F10.wireOp",EDGE,"E11.1"),sQuery(id+"F10.wireOp",EDGE,"E11.2"),sQuery(id+"F10.wireOp",EDGE,"E11.3"),sQuery(id+"F10.wireOp",EDGE,"E11.4"),sQuery(id+"F10.wireOp",EDGE,"E11.5")])]}),"instanceName":"1"}),"instanceName":"1"});
            var Q1;
            Q1=makeQuery(id+"F15.opPattern","COPY",BODY,{"derivedFrom":makeQuery(id+"F11.opExtrude","SWEPT_BODY",BODY,{"disambiguationData":[OSD([sQuery(id+"F10.wireOp",EDGE,"E11.0"),sQuery(id+"F10.wireOp",EDGE,"E11.1"),sQuery(id+"F10.wireOp",EDGE,"E11.2"),sQuery(id+"F10.wireOp",EDGE,"E11.3"),sQuery(id+"F10.wireOp",EDGE,"E11.4"),sQuery(id+"F10.wireOp",EDGE,"E11.5")])]}),"instanceName":"1"});
            var Q2;
            Q2=makeQuery(id+"F21.opPattern","COPY",BODY,{"derivedFrom":makeQuery(id+"F15.opPattern","COPY",BODY,{"derivedFrom":makeQuery(id+"F11.opExtrude","SWEPT_BODY",BODY,{"disambiguationData":[OSD([sQuery(id+"F10.wireOp",EDGE,"E11.0"),sQuery(id+"F10.wireOp",EDGE,"E11.1"),sQuery(id+"F10.wireOp",EDGE,"E11.2"),sQuery(id+"F10.wireOp",EDGE,"E11.3"),sQuery(id+"F10.wireOp",EDGE,"E11.4"),sQuery(id+"F10.wireOp",EDGE,"E11.5")])]}),"instanceName":"1"}),"instanceName":"1"});
            var Q3;
            Q3=makeQuery(id+"F22.opPattern","COPY",BODY,{"derivedFrom":makeQuery(id+"F21.opPattern","COPY",BODY,{"derivedFrom":makeQuery(id+"F11.opExtrude","SWEPT_BODY",BODY,{"disambiguationData":[OSD([sQuery(id+"F10.wireOp",EDGE,"E11.0"),sQuery(id+"F10.wireOp",EDGE,"E11.1"),sQuery(id+"F10.wireOp",EDGE,"E11.2"),sQuery(id+"F10.wireOp",EDGE,"E11.3"),sQuery(id+"F10.wireOp",EDGE,"E11.4"),sQuery(id+"F10.wireOp",EDGE,"E11.5")])]}),"instanceName":"1"}),"instanceName":"1"});
            var Q4;
            Q4=makeQuery(id+"F22.opPattern","COPY",BODY,{"derivedFrom":makeQuery(id+"F15.opPattern","COPY",BODY,{"derivedFrom":makeQuery(id+"F14.opPattern","COPY",BODY,{"derivedFrom":makeQuery(id+"F11.opExtrude","SWEPT_BODY",BODY,{"disambiguationData":[OSD([sQuery(id+"F10.wireOp",EDGE,"E11.0"),sQuery(id+"F10.wireOp",EDGE,"E11.1"),sQuery(id+"F10.wireOp",EDGE,"E11.2"),sQuery(id+"F10.wireOp",EDGE,"E11.3"),sQuery(id+"F10.wireOp",EDGE,"E11.4"),sQuery(id+"F10.wireOp",EDGE,"E11.5")])]}),"instanceName":"1"}),"instanceName":"1"}),"instanceName":"1"});
            var Q5;
            Q5=makeQuery(id+"F22.opPattern","COPY",BODY,{"derivedFrom":makeQuery(id+"F11.opExtrude","SWEPT_BODY",BODY,{"disambiguationData":[OSD([sQuery(id+"F10.wireOp",EDGE,"E11.0"),sQuery(id+"F10.wireOp",EDGE,"E11.1"),sQuery(id+"F10.wireOp",EDGE,"E11.2"),sQuery(id+"F10.wireOp",EDGE,"E11.3"),sQuery(id+"F10.wireOp",EDGE,"E11.4"),sQuery(id+"F10.wireOp",EDGE,"E11.5")])]}),"instanceName":"1"});
            var Q6;
            Q6=makeQuery(id+"F22.opPattern","COPY",BODY,{"derivedFrom":makeQuery(id+"F17.opPattern","COPY",BODY,{"derivedFrom":makeQuery(id+"F15.opPattern","COPY",BODY,{"derivedFrom":makeQuery(id+"F14.opPattern","COPY",BODY,{"derivedFrom":makeQuery(id+"F11.opExtrude","SWEPT_BODY",BODY,{"disambiguationData":[OSD([sQuery(id+"F10.wireOp",EDGE,"E11.0"),sQuery(id+"F10.wireOp",EDGE,"E11.1"),sQuery(id+"F10.wireOp",EDGE,"E11.2"),sQuery(id+"F10.wireOp",EDGE,"E11.3"),sQuery(id+"F10.wireOp",EDGE,"E11.4"),sQuery(id+"F10.wireOp",EDGE,"E11.5")])]}),"instanceName":"1"}),"instanceName":"1"}),"instanceName":"1"}),"instanceName":"1"});
            var Q7;
            Q7=makeQuery(id+"F22.opPattern","COPY",BODY,{"derivedFrom":makeQuery(id+"F17.opPattern","COPY",BODY,{"derivedFrom":makeQuery(id+"F11.opExtrude","SWEPT_BODY",BODY,{"disambiguationData":[OSD([sQuery(id+"F10.wireOp",EDGE,"E11.0"),sQuery(id+"F10.wireOp",EDGE,"E11.1"),sQuery(id+"F10.wireOp",EDGE,"E11.2"),sQuery(id+"F10.wireOp",EDGE,"E11.3"),sQuery(id+"F10.wireOp",EDGE,"E11.4"),sQuery(id+"F10.wireOp",EDGE,"E11.5")])]}),"instanceName":"1"}),"instanceName":"1"});
            var Q8;
            Q8=makeQuery(id+"F21.opPattern","COPY",BODY,{"derivedFrom":makeQuery(id+"F16.opPattern","COPY",BODY,{"derivedFrom":makeQuery(id+"F15.opPattern","COPY",BODY,{"derivedFrom":makeQuery(id+"F11.opExtrude","SWEPT_BODY",BODY,{"disambiguationData":[OSD([sQuery(id+"F10.wireOp",EDGE,"E11.0"),sQuery(id+"F10.wireOp",EDGE,"E11.1"),sQuery(id+"F10.wireOp",EDGE,"E11.2"),sQuery(id+"F10.wireOp",EDGE,"E11.3"),sQuery(id+"F10.wireOp",EDGE,"E11.4"),sQuery(id+"F10.wireOp",EDGE,"E11.5")])]}),"instanceName":"1"}),"instanceName":"1"}),"instanceName":"1"});
            transform(context, id + "F23", {"entities" : qUnion([Q0, Q1, Q2, Q3, Q4, Q5, Q6, Q7, Q8]), "transformType" : TransformType.TRANSLATION_3D, "dx" : -9.9 * mm, "dy" : -0.64 * mm, "dz" : 0 * mm, "makeCopy" : true});
        }
        {
            var Q0;
            Q0=makeQuery(id+"F22.opPattern","COPY",BODY,{"derivedFrom":makeQuery(id+"F18.opPattern","COPY",BODY,{"derivedFrom":makeQuery(id+"F17.opPattern","COPY",BODY,{"derivedFrom":makeQuery(id+"F15.opPattern","COPY",BODY,{"derivedFrom":makeQuery(id+"F14.opPattern","COPY",BODY,{"derivedFrom":makeQuery(id+"F11.opExtrude","SWEPT_BODY",BODY,{"disambiguationData":[OSD([sQuery(id+"F10.wireOp",EDGE,"E11.0"),sQuery(id+"F10.wireOp",EDGE,"E11.1"),sQuery(id+"F10.wireOp",EDGE,"E11.2"),sQuery(id+"F10.wireOp",EDGE,"E11.3"),sQuery(id+"F10.wireOp",EDGE,"E11.4"),sQuery(id+"F10.wireOp",EDGE,"E11.5")])]}),"instanceName":"1"}),"instanceName":"1"}),"instanceName":"1"}),"instanceName":"1"}),"instanceName":"1"});
            transform(context, id + "F24", {"entities" : qUnion([Q0]), "transformType" : TransformType.TRANSLATION_3D, "dx" : -5.1 * mm, "dy" : 2.54 * mm, "dz" : 0 * mm, "makeCopy" : true});
        }
    });
